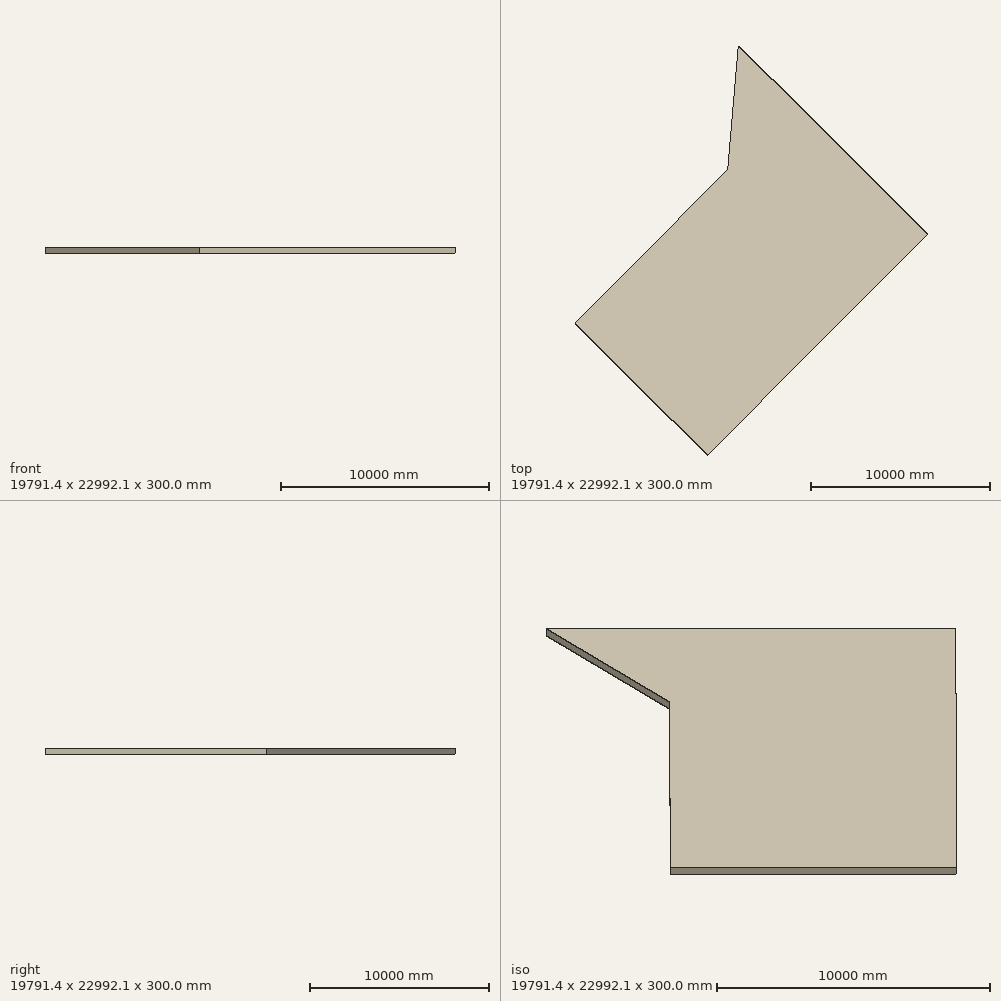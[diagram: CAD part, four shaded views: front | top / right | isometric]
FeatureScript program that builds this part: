
annotation { "Feature Type Name" : "Feature", "Feature Type Description" : "" }
export const myFeature = defineFeature(function(context is Context, id is Id, definition is map)
    precondition{}
    {
        {
            var Q0;
            Q0=qCreatedBy(makeId("Top.planeOp"),FACE);
            var sketch = newSketch(context, id + "F0", { "sketchPlane" : qUnion([Q0])});
            skLineSegment(sketch, "E0", {"start": v(-10631.28, 10598.87) * mm, "end": v(0, 0) * mm});
            skLineSegment(sketch, "E1", {"start": v(0, 0) * mm, "end": v(-12355.46, -12393.25) * mm});
            skLineSegment(sketch, "E2", {"start": v(-12355.46, -12393.25) * mm, "end": v(-19791.41, -4979.97) * mm});
            skLineSegment(sketch, "E3", {"start": v(-19791.41, -4979.97) * mm, "end": v(-11232.25, 3605.36) * mm});
            skLineSegment(sketch, "E4", {"start": v(-11232.25, 3605.36) * mm, "end": v(-10631.28, 10598.87) * mm});
            skSolve(sketch);
        }
        {
            var Q0;
            Q0=makeQuery(id+"F0.imprint","IMPRINT",FACE,{"disambiguationData":[TD([[makeQuery(id+"F0.imprint","IMPRINT",EDGE,{"derivedFrom":sQuery(id+"F0.wireOp",EDGE,"E0")}),-1.0]])]});
            extrude(context, id + "F1", {"entities" : qUnion([Q0]), "depth" : 300 * mm});
        }
    });
